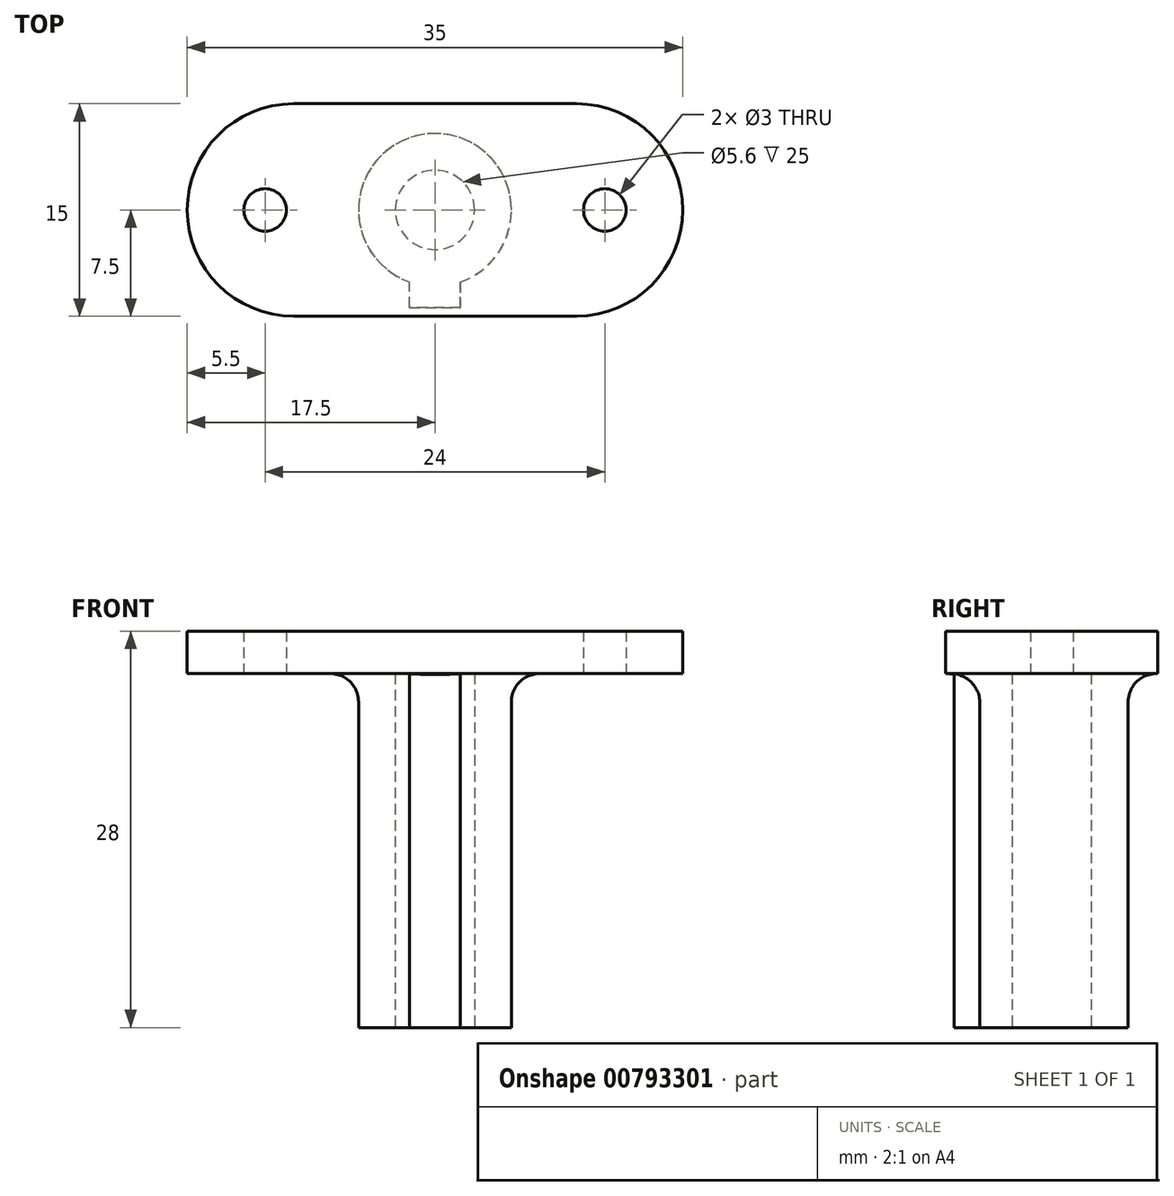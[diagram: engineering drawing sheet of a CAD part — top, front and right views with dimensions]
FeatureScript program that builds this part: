
annotation { "Feature Type Name" : "Feature", "Feature Type Description" : "" }
export const myFeature = defineFeature(function(context is Context, id is Id, definition is map)
    precondition{}
    {
        {
            var Q0;
            Q0=qCreatedBy(makeId("Top.planeOp"),FACE);
            var sketch = newSketch(context, id + "F0", { "sketchPlane" : qUnion([Q0])});
            skCircle(sketch, "E0", {"center": v(0, 0) * mm, "radius": 5.4 * mm});
            skLineSegment(sketch, "E1.bottom", {"start": v(-1.8, -6.9) * mm, "end": v(1.8, -6.9) * mm});
            skLineSegment(sketch, "E1.top", {"start": v(-1.8, -3.1) * mm, "end": v(1.8, -3.1) * mm});
            skLineSegment(sketch, "E1.left", {"start": v(-1.8, -6.9) * mm, "end": v(-1.8, -3.1) * mm});
            skLineSegment(sketch, "E1.right", {"start": v(1.8, -6.9) * mm, "end": v(1.8, -3.1) * mm});
            skCircle(sketch, "E2", {"center": v(0, 0) * mm, "radius": 2.8 * mm});
            skSolve(sketch);
        }
        {
            var Q0;
            Q0 = qSketchRegion(id + "F0", true);
            extrude(context, id + "F1", {"entities" : qUnion([Q0]), "depth" : 25 * mm, "offsetDistance" : 25 * mm});
        }
        {
            var Q0;
            Q0=makeQuery(id+"F1.opExtrude","CAP_FACE",FACE,{"disambiguationData":[OSD([sQuery(id+"F0.wireOp",EDGE,"E0"),sQuery(id+"F0.wireOp",EDGE,"E1.bottom"),sQuery(id+"F0.wireOp",EDGE,"E1.left"),sQuery(id+"F0.wireOp",EDGE,"E1.right"),sQuery(id+"F0.wireOp",EDGE,"E2")])],"isStart":false});
            var sketch = newSketch(context, id + "F2", { "sketchPlane" : qUnion([Q0])});
            skLineSegment(sketch, "E3.bottom", {"start": v(10, 7.5) * mm, "end": v(-10, 7.5) * mm});
            skLineSegment(sketch, "E3.top", {"start": v(10, -7.5) * mm, "end": v(-10, -7.5) * mm});
            skLineSegment(sketch, "E3.left", {"start": v(17.5, 0) * mm, "end": v(17.5, 0) * mm});
            skLineSegment(sketch, "E3.right", {"start": v(-17.5, 0) * mm, "end": v(-17.5, 0) * mm});
            skPoint(sketch, "E3.middle", {"position": v(0, 0) * mm});
            skCircle(sketch, "E4", {"center": v(-12, 0) * mm, "radius": 1.5 * mm});
            skCircle(sketch, "E5", {"center": v(12, 0) * mm, "radius": 1.5 * mm});
            skPoint(sketch, "E6.visualSharp", {"position": v(-17.5, 7.5) * mm});
            skArc(sketch, "E6.filletArc", {"start": v(-10, 7.5) * mm, "mid": v(-15.3, 5.3) * mm, "end": v(-17.5, 0) * mm});
            skPoint(sketch, "E7.visualSharp", {"position": v(17.5, 7.5) * mm});
            skArc(sketch, "E7.filletArc", {"start": v(17.5, 0) * mm, "mid": v(15.3, 5.3) * mm, "end": v(10, 7.5) * mm});
            skPoint(sketch, "E8.visualSharp", {"position": v(17.5, -7.5) * mm});
            skArc(sketch, "E8.filletArc", {"start": v(10, -7.5) * mm, "mid": v(15.3, -5.3) * mm, "end": v(17.5, 0) * mm});
            skPoint(sketch, "E9.visualSharp", {"position": v(-17.5, -7.5) * mm});
            skArc(sketch, "E9.filletArc", {"start": v(-17.5, 0) * mm, "mid": v(-15.3, -5.3) * mm, "end": v(-10, -7.5) * mm});
            skSolve(sketch);
        }
        {
            var Q0;
            Q0 = qSketchRegion(id + "F2", true);
            extrude(context, id + "F3", {"entities" : qUnion([Q0]), "operationType" : NewBodyOperationType.ADD, "depth" : 3 * mm, "offsetDistance" : 25 * mm});
        }
        {
            var Q0;
            Q0=makeQuery(id+"F1.opExtrude","CAP_EDGE",EDGE,{"disambiguationData":[OSD([sQuery(id+"F0.wireOp",EDGE,"E0")])],"isStart":false});
            fillet(context, id + "F4", {"entities" : qUnion([Q0]), "radius" : 2 * mm, "tangentPropagation" : true, "allowEdgeOverflow" : false});
        }
    });
